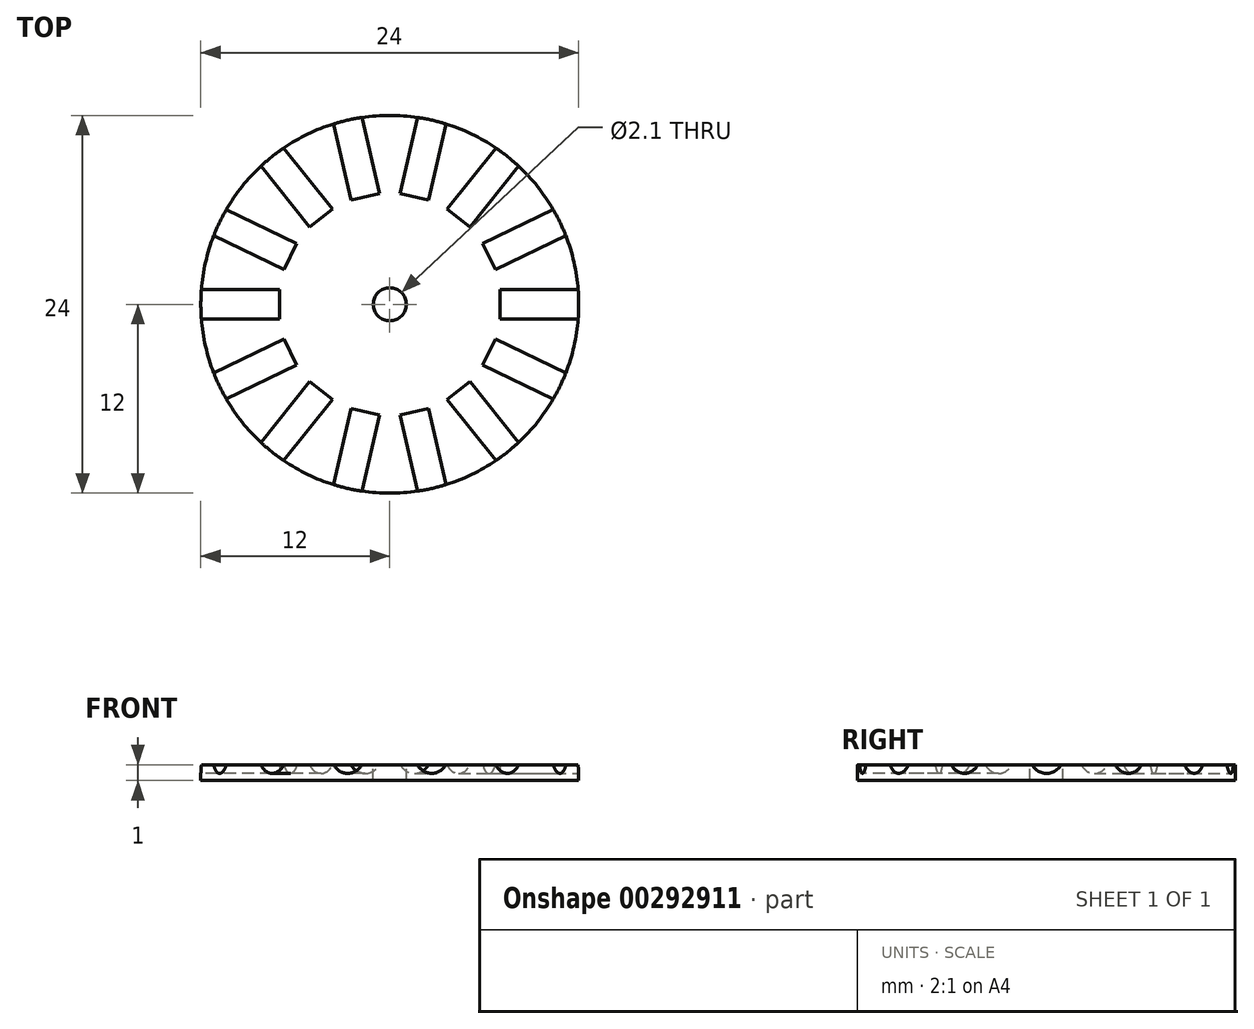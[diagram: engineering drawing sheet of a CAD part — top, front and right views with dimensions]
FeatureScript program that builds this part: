
annotation { "Feature Type Name" : "Feature", "Feature Type Description" : "" }
export const myFeature = defineFeature(function(context is Context, id is Id, definition is map)
    precondition{}
    {
        {
            var Q0;
            Q0=qCreatedBy(makeId("Top.planeOp"),FACE);
            var sketch = newSketch(context, id + "F0", { "sketchPlane" : qUnion([Q0])});
            skCircle(sketch, "E0", {"center": v(0, 0) * mm, "radius": 12 * mm});
            skSolve(sketch);
        }
        {
            var Q0;
            Q0=makeQuery(id+"F0.imprint","IMPRINT",FACE,{"disambiguationData":[TD([[makeQuery(id+"F0.imprint","IMPRINT",EDGE,{"derivedFrom":sQuery(id+"F0.wireOp",EDGE,"E0")}),1.0]])]});
            extrude(context, id + "F1", {"entities" : qUnion([Q0]), "depth" : 1 * mm});
        }
        {
            var Q0;
            Q0=makeQuery(id+"F1.opExtrude","CAP_FACE",FACE,{"disambiguationData":[OSD([sQuery(id+"F0.wireOp",EDGE,"E0")])],"isStart":false});
            var sketch = newSketch(context, id + "F2", { "sketchPlane" : qUnion([Q0])});
            skCircle(sketch, "E1", {"center": v(0, 0) * mm, "radius": 1.05 * mm});
            skSolve(sketch);
        }
        {
            var Q0;
            Q0=makeQuery(id+"F2.imprint","IMPRINT",FACE,{"disambiguationData":[TD([[makeQuery(id+"F2.imprint","IMPRINT",EDGE,{"derivedFrom":sQuery(id+"F2.wireOp",EDGE,"E1")}),1.0]])]});
            var Q1;
            Q1=sQuery(id+"F2.wireOp",EDGE,"E1");
            extrude(context, id + "F3", {"entities" : qUnion([Q0]), "operationType" : NewBodyOperationType.REMOVE, "surfaceEntities" : qUnion([Q1]), "oppositeDirection" : true, "depth" : 25 * mm});
        }
        {
            var Q0;
            Q0=qCreatedBy(makeId("Front.planeOp"),FACE);
            var sketch = newSketch(context, id + "F4", { "sketchPlane" : qUnion([Q0])});
            skLineSegment(sketch, "E2", {"start": v(0, 0) * mm, "end": v(0, 13.37) * mm, "construction": true});
            skSolve(sketch);
        }
        {
            var Q0;
            Q0=qCreatedBy(makeId("Right.planeOp"),FACE);
            cPlane(context, id + "F5", {"entities" : qUnion([Q0]), "cplaneType" : CPlaneType.OFFSET, "offset" : 12 * mm, "width" : 150 * mm, "height" : 150 * mm});
        }
        {
            var Q0;
            Q0=qCreatedBy(id+"F5.planeOp",FACE);
            var sketch = newSketch(context, id + "F6", { "sketchPlane" : qUnion([Q0])});
            skLineSegment(sketch, "E3", {"start": v(0, 0) * mm, "end": v(0, 1.5) * mm, "construction": true});
            skCircle(sketch, "E4", {"center": v(0, 1.5) * mm, "radius": 1.05 * mm});
            skLineSegment(sketch, "E5", {"start": v(-0.95, 1.06) * mm, "end": v(0.95, 1.06) * mm});
            skSolve(sketch);
        }
        {
            var Q0;
            Q0=qSketchRegion(id+"F6",true);
            extrude(context, id + "F7", {"entities" : qUnion([Q0]), "oppositeDirection" : true, "depth" : 5 * mm});
        }
        {
            var Q0;
            Q0=makeQuery(id+"F7.opExtrude","SWEPT_BODY",BODY,{"disambiguationData":[OSD([sQuery(id+"F6.wireOp",EDGE,"E4")])]});
            var Q1;
            Q1=sQuery(id+"F4.wireOp",EDGE,"E2");
            circularPattern(context, id + "F8", {"operationType" : NewBodyOperationType.REMOVE, "entities" : qUnion([Q0]), "axis" : qUnion([Q1]), "angle" : 360 * degree, "instanceCount" : 14, "equalSpace" : true});
        }
    });
